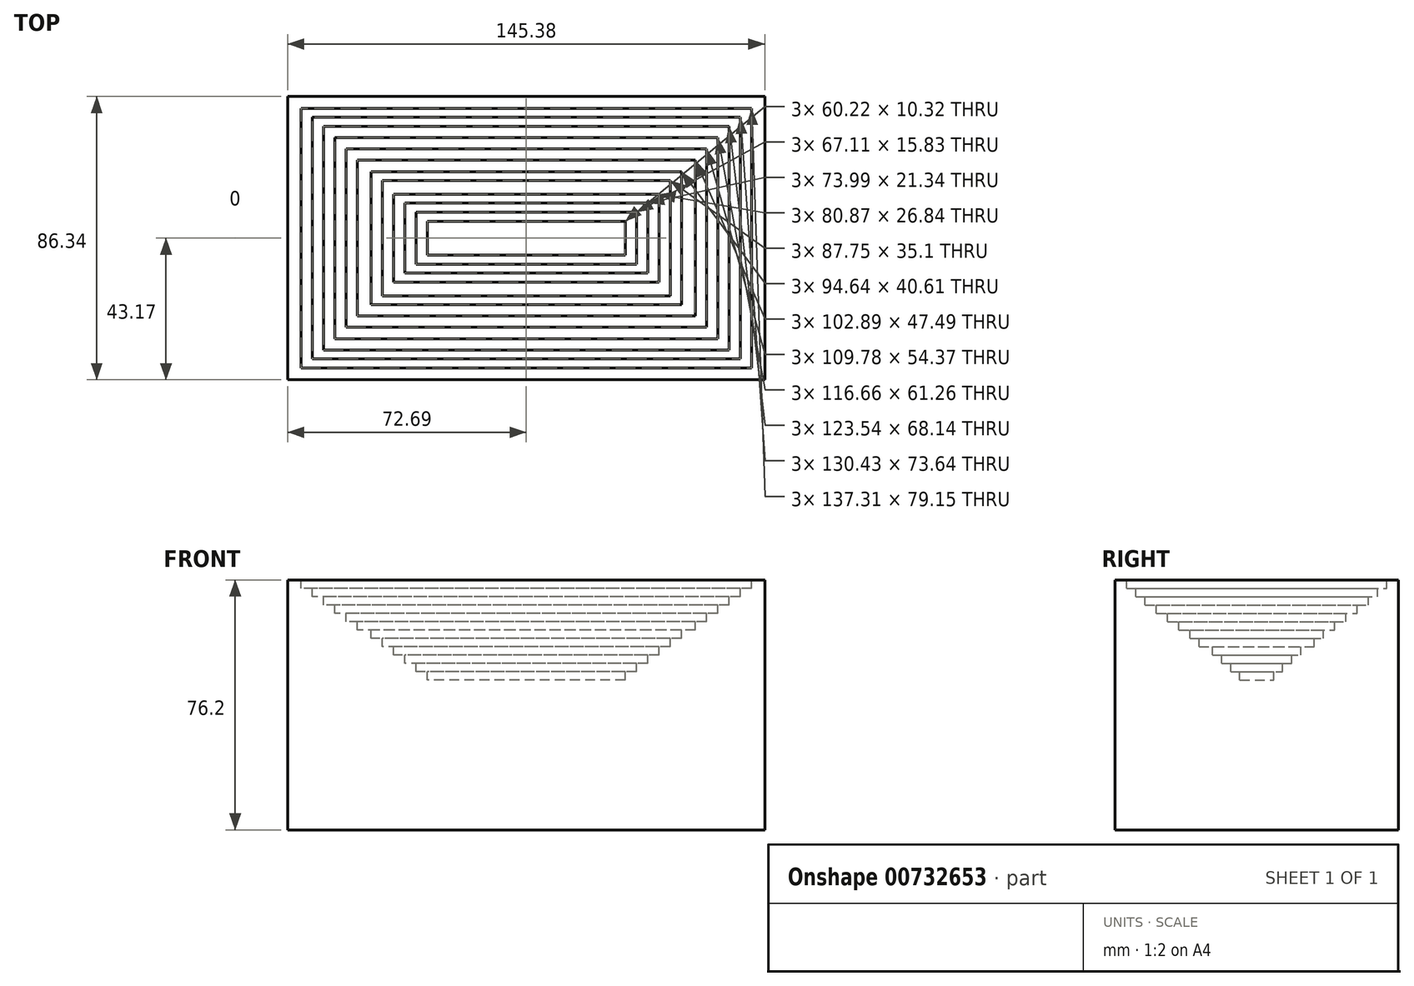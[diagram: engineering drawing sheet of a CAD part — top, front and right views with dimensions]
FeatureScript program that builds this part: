
annotation { "Feature Type Name" : "Feature", "Feature Type Description" : "" }
export const myFeature = defineFeature(function(context is Context, id is Id, definition is map)
    precondition{}
    {
        {
            var Q0;
            Q0=qCreatedBy(makeId("Top.planeOp"),FACE);
            var sketch = newSketch(context, id + "F0", { "sketchPlane" : qUnion([Q0])});
            skLineSegment(sketch, "E0.bottom", {"start": v(72.7, -43.17) * mm, "end": v(-72.7, -43.17) * mm});
            skLineSegment(sketch, "E0.top", {"start": v(72.7, 43.17) * mm, "end": v(-72.7, 43.17) * mm});
            skLineSegment(sketch, "E0.left", {"start": v(72.7, -43.17) * mm, "end": v(72.7, 43.17) * mm});
            skLineSegment(sketch, "E0.right", {"start": v(-72.7, -43.17) * mm, "end": v(-72.7, 43.17) * mm});
            skPoint(sketch, "E0.middle", {"position": v(0, 0) * mm});
            skSolve(sketch);
        }
        {
            var Q0;
            Q0=makeQuery(id+"F0.imprint","IMPRINT",FACE,{"disambiguationData":[TD([[makeQuery(id+"F0.imprint","IMPRINT",EDGE,{"derivedFrom":sQuery(id+"F0.wireOp",EDGE,"E0.bottom")}),-1.0]])]});
            extrude(context, id + "F1", {"entities" : qUnion([Q0]), "depth" : 76.2 * mm, "offsetDistance" : 25.4 * mm});
        }
        {
            var Q0;
            Q0=makeQuery(id+"F1.opExtrude","CAP_FACE",FACE,{"disambiguationData":[OSD([sQuery(id+"F0.wireOp",EDGE,"E0.bottom"),sQuery(id+"F0.wireOp",EDGE,"E0.top"),sQuery(id+"F0.wireOp",EDGE,"E0.left"),sQuery(id+"F0.wireOp",EDGE,"E0.right")])],"isStart":false});
            var sketch = newSketch(context, id + "F2", { "sketchPlane" : qUnion([Q0])});
            skLineSegment(sketch, "E1.bottom", {"start": v(68.65, -39.57) * mm, "end": v(-68.65, -39.57) * mm});
            skLineSegment(sketch, "E1.top", {"start": v(68.65, 39.57) * mm, "end": v(-68.65, 39.57) * mm});
            skLineSegment(sketch, "E1.left", {"start": v(68.65, -39.57) * mm, "end": v(68.65, 39.57) * mm});
            skLineSegment(sketch, "E1.right", {"start": v(-68.65, -39.57) * mm, "end": v(-68.65, 39.57) * mm});
            skPoint(sketch, "E1.middle", {"position": v(0, 0) * mm});
            skSolve(sketch);
        }
        {
            var Q0;
            Q0=makeQuery(id+"F2.imprint","IMPRINT",FACE,{"disambiguationData":[TD([[makeQuery(id+"F2.imprint","IMPRINT",EDGE,{"derivedFrom":sQuery(id+"F2.wireOp",EDGE,"E1.bottom")}),-1.0]])]});
            extrude(context, id + "F3", {"entities" : qUnion([Q0]), "operationType" : NewBodyOperationType.REMOVE, "oppositeDirection" : true, "depth" : 2.54 * mm, "offsetDistance" : 25.4 * mm});
        }
        {
            var Q0;
            Q0=makeQuery(id+"F3.boolean.opBoolean","COPY",FACE,{"derivedFrom":makeQuery(id+"F3.opExtrude","CAP_FACE",FACE,{"disambiguationData":[OSD([sQuery(id+"F2.wireOp",EDGE,"E1.bottom"),sQuery(id+"F2.wireOp",EDGE,"E1.top"),sQuery(id+"F2.wireOp",EDGE,"E1.left"),sQuery(id+"F2.wireOp",EDGE,"E1.right")])],"isStart":false})});
            var sketch = newSketch(context, id + "F4", { "sketchPlane" : qUnion([Q0])});
            skLineSegment(sketch, "E2.bottom", {"start": v(65.21, -36.82) * mm, "end": v(-65.21, -36.82) * mm});
            skLineSegment(sketch, "E2.top", {"start": v(65.21, 36.82) * mm, "end": v(-65.21, 36.82) * mm});
            skLineSegment(sketch, "E2.left", {"start": v(65.21, -36.82) * mm, "end": v(65.21, 36.82) * mm});
            skLineSegment(sketch, "E2.right", {"start": v(-65.21, -36.82) * mm, "end": v(-65.21, 36.82) * mm});
            skPoint(sketch, "E2.middle", {"position": v(0, 0) * mm});
            skSolve(sketch);
        }
        {
            var Q0;
            Q0=makeQuery(id+"F4.imprint","IMPRINT",FACE,{"disambiguationData":[TD([[makeQuery(id+"F4.imprint","IMPRINT",EDGE,{"derivedFrom":sQuery(id+"F4.wireOp",EDGE,"E2.bottom")}),-1.0]])]});
            extrude(context, id + "F5", {"entities" : qUnion([Q0]), "operationType" : NewBodyOperationType.REMOVE, "oppositeDirection" : true, "depth" : 2.54 * mm, "offsetDistance" : 25.4 * mm});
        }
        {
            var Q0;
            Q0=makeQuery(id+"F5.boolean.opBoolean","COPY",FACE,{"derivedFrom":makeQuery(id+"F5.opExtrude","CAP_FACE",FACE,{"disambiguationData":[OSD([sQuery(id+"F4.wireOp",EDGE,"E2.bottom"),sQuery(id+"F4.wireOp",EDGE,"E2.top"),sQuery(id+"F4.wireOp",EDGE,"E2.left"),sQuery(id+"F4.wireOp",EDGE,"E2.right")])],"isStart":false})});
            var sketch = newSketch(context, id + "F6", { "sketchPlane" : qUnion([Q0])});
            skLineSegment(sketch, "E3.bottom", {"start": v(61.77, -34.07) * mm, "end": v(-61.77, -34.07) * mm});
            skLineSegment(sketch, "E3.top", {"start": v(61.77, 34.07) * mm, "end": v(-61.77, 34.07) * mm});
            skLineSegment(sketch, "E3.left", {"start": v(61.77, -34.07) * mm, "end": v(61.77, 34.07) * mm});
            skLineSegment(sketch, "E3.right", {"start": v(-61.77, -34.07) * mm, "end": v(-61.77, 34.07) * mm});
            skPoint(sketch, "E3.middle", {"position": v(0, 0) * mm});
            skSolve(sketch);
        }
        {
            var Q0;
            Q0=makeQuery(id+"F6.imprint","IMPRINT",FACE,{"disambiguationData":[TD([[makeQuery(id+"F6.imprint","IMPRINT",EDGE,{"derivedFrom":sQuery(id+"F6.wireOp",EDGE,"E3.bottom")}),-1.0]])]});
            extrude(context, id + "F7", {"entities" : qUnion([Q0]), "operationType" : NewBodyOperationType.REMOVE, "oppositeDirection" : true, "depth" : 2.54 * mm, "offsetDistance" : 25.4 * mm});
        }
        {
            var Q0;
            Q0=makeQuery(id+"F7.boolean.opBoolean","COPY",FACE,{"derivedFrom":makeQuery(id+"F7.opExtrude","CAP_FACE",FACE,{"disambiguationData":[OSD([sQuery(id+"F6.wireOp",EDGE,"E3.bottom"),sQuery(id+"F6.wireOp",EDGE,"E3.top"),sQuery(id+"F6.wireOp",EDGE,"E3.left"),sQuery(id+"F6.wireOp",EDGE,"E3.right")])],"isStart":false})});
            var sketch = newSketch(context, id + "F8", { "sketchPlane" : qUnion([Q0])});
            skLineSegment(sketch, "E4.bottom", {"start": v(58.33, -30.63) * mm, "end": v(-58.33, -30.63) * mm});
            skLineSegment(sketch, "E4.top", {"start": v(58.33, 30.63) * mm, "end": v(-58.33, 30.63) * mm});
            skLineSegment(sketch, "E4.left", {"start": v(58.33, -30.63) * mm, "end": v(58.33, 30.63) * mm});
            skLineSegment(sketch, "E4.right", {"start": v(-58.33, -30.63) * mm, "end": v(-58.33, 30.63) * mm});
            skPoint(sketch, "E4.middle", {"position": v(0, 0) * mm});
            skSolve(sketch);
        }
        {
            var Q0;
            Q0=makeQuery(id+"F8.imprint","IMPRINT",FACE,{"disambiguationData":[TD([[makeQuery(id+"F8.imprint","IMPRINT",EDGE,{"derivedFrom":sQuery(id+"F8.wireOp",EDGE,"E4.bottom")}),-1.0]])]});
            extrude(context, id + "F9", {"entities" : qUnion([Q0]), "operationType" : NewBodyOperationType.REMOVE, "oppositeDirection" : true, "depth" : 2.54 * mm, "offsetDistance" : 25.4 * mm});
        }
        {
            var Q0;
            Q0=makeQuery(id+"F9.boolean.opBoolean","COPY",FACE,{"derivedFrom":makeQuery(id+"F9.opExtrude","CAP_FACE",FACE,{"disambiguationData":[OSD([sQuery(id+"F8.wireOp",EDGE,"E4.bottom"),sQuery(id+"F8.wireOp",EDGE,"E4.top"),sQuery(id+"F8.wireOp",EDGE,"E4.left"),sQuery(id+"F8.wireOp",EDGE,"E4.right")])],"isStart":false})});
            var sketch = newSketch(context, id + "F10", { "sketchPlane" : qUnion([Q0])});
            skLineSegment(sketch, "E5.bottom", {"start": v(54.89, -27.19) * mm, "end": v(-54.89, -27.19) * mm});
            skLineSegment(sketch, "E5.top", {"start": v(54.89, 27.19) * mm, "end": v(-54.89, 27.19) * mm});
            skLineSegment(sketch, "E5.left", {"start": v(54.89, -27.19) * mm, "end": v(54.89, 27.19) * mm});
            skLineSegment(sketch, "E5.right", {"start": v(-54.89, -27.19) * mm, "end": v(-54.89, 27.19) * mm});
            skPoint(sketch, "E5.middle", {"position": v(0, 0) * mm});
            skSolve(sketch);
        }
        {
            var Q0;
            Q0=makeQuery(id+"F10.imprint","IMPRINT",FACE,{"disambiguationData":[TD([[makeQuery(id+"F10.imprint","IMPRINT",EDGE,{"derivedFrom":sQuery(id+"F10.wireOp",EDGE,"E5.bottom")}),-1.0]])]});
            extrude(context, id + "F11", {"entities" : qUnion([Q0]), "operationType" : NewBodyOperationType.REMOVE, "oppositeDirection" : true, "depth" : 2.54 * mm, "offsetDistance" : 25.4 * mm});
        }
        {
            var Q0;
            Q0=makeQuery(id+"F11.boolean.opBoolean","COPY",FACE,{"derivedFrom":makeQuery(id+"F11.opExtrude","CAP_FACE",FACE,{"disambiguationData":[OSD([sQuery(id+"F10.wireOp",EDGE,"E5.bottom"),sQuery(id+"F10.wireOp",EDGE,"E5.top"),sQuery(id+"F10.wireOp",EDGE,"E5.left"),sQuery(id+"F10.wireOp",EDGE,"E5.right")])],"isStart":false})});
            var sketch = newSketch(context, id + "F12", { "sketchPlane" : qUnion([Q0])});
            skLineSegment(sketch, "E6.bottom", {"start": v(51.45, -23.74) * mm, "end": v(-51.45, -23.74) * mm});
            skLineSegment(sketch, "E6.top", {"start": v(51.45, 23.74) * mm, "end": v(-51.45, 23.74) * mm});
            skLineSegment(sketch, "E6.left", {"start": v(51.45, -23.74) * mm, "end": v(51.45, 23.74) * mm});
            skLineSegment(sketch, "E6.right", {"start": v(-51.45, -23.74) * mm, "end": v(-51.45, 23.74) * mm});
            skPoint(sketch, "E6.middle", {"position": v(0, 0) * mm});
            skSolve(sketch);
        }
        {
            var Q0;
            Q0=makeQuery(id+"F12.imprint","IMPRINT",FACE,{"disambiguationData":[TD([[makeQuery(id+"F12.imprint","IMPRINT",EDGE,{"derivedFrom":sQuery(id+"F12.wireOp",EDGE,"E6.bottom")}),-1.0]])]});
            extrude(context, id + "F13", {"entities" : qUnion([Q0]), "operationType" : NewBodyOperationType.REMOVE, "oppositeDirection" : true, "depth" : 2.54 * mm, "offsetDistance" : 25.4 * mm});
        }
        {
            var Q0;
            Q0=makeQuery(id+"F13.boolean.opBoolean","COPY",FACE,{"derivedFrom":makeQuery(id+"F13.opExtrude","CAP_FACE",FACE,{"disambiguationData":[OSD([sQuery(id+"F12.wireOp",EDGE,"E6.bottom"),sQuery(id+"F12.wireOp",EDGE,"E6.top"),sQuery(id+"F12.wireOp",EDGE,"E6.left"),sQuery(id+"F12.wireOp",EDGE,"E6.right")])],"isStart":false})});
            var sketch = newSketch(context, id + "F14", { "sketchPlane" : qUnion([Q0])});
            skLineSegment(sketch, "E7.bottom", {"start": v(47.32, -20.3) * mm, "end": v(-47.32, -20.3) * mm});
            skLineSegment(sketch, "E7.top", {"start": v(47.32, 20.3) * mm, "end": v(-47.32, 20.3) * mm});
            skLineSegment(sketch, "E7.left", {"start": v(47.32, -20.3) * mm, "end": v(47.32, 20.3) * mm});
            skLineSegment(sketch, "E7.right", {"start": v(-47.32, -20.3) * mm, "end": v(-47.32, 20.3) * mm});
            skPoint(sketch, "E7.middle", {"position": v(0, 0) * mm});
            skSolve(sketch);
        }
        {
            var Q0;
            Q0=makeQuery(id+"F14.imprint","IMPRINT",FACE,{"disambiguationData":[TD([[makeQuery(id+"F14.imprint","IMPRINT",EDGE,{"derivedFrom":sQuery(id+"F14.wireOp",EDGE,"E7.bottom")}),-1.0]])]});
            extrude(context, id + "F15", {"entities" : qUnion([Q0]), "operationType" : NewBodyOperationType.REMOVE, "oppositeDirection" : true, "depth" : 2.54 * mm, "offsetDistance" : 25.4 * mm});
        }
        {
            var Q0;
            Q0=makeQuery(id+"F15.boolean.opBoolean","COPY",FACE,{"derivedFrom":makeQuery(id+"F15.opExtrude","CAP_FACE",FACE,{"disambiguationData":[OSD([sQuery(id+"F14.wireOp",EDGE,"E7.bottom"),sQuery(id+"F14.wireOp",EDGE,"E7.top"),sQuery(id+"F14.wireOp",EDGE,"E7.left"),sQuery(id+"F14.wireOp",EDGE,"E7.right")])],"isStart":false})});
            var sketch = newSketch(context, id + "F16", { "sketchPlane" : qUnion([Q0])});
            skLineSegment(sketch, "E8.bottom", {"start": v(43.88, -17.55) * mm, "end": v(-43.88, -17.55) * mm});
            skLineSegment(sketch, "E8.top", {"start": v(43.88, 17.55) * mm, "end": v(-43.88, 17.55) * mm});
            skLineSegment(sketch, "E8.left", {"start": v(43.88, -17.55) * mm, "end": v(43.88, 17.55) * mm});
            skLineSegment(sketch, "E8.right", {"start": v(-43.88, -17.55) * mm, "end": v(-43.88, 17.55) * mm});
            skPoint(sketch, "E8.middle", {"position": v(0, 0) * mm});
            skSolve(sketch);
        }
        {
            var Q0;
            Q0=makeQuery(id+"F16.imprint","IMPRINT",FACE,{"disambiguationData":[TD([[makeQuery(id+"F16.imprint","IMPRINT",EDGE,{"derivedFrom":sQuery(id+"F16.wireOp",EDGE,"E8.bottom")}),-1.0]])]});
            extrude(context, id + "F17", {"entities" : qUnion([Q0]), "operationType" : NewBodyOperationType.REMOVE, "oppositeDirection" : true, "depth" : 2.54 * mm, "offsetDistance" : 25.4 * mm});
        }
        {
            var Q0;
            Q0=makeQuery(id+"F17.boolean.opBoolean","COPY",FACE,{"derivedFrom":makeQuery(id+"F17.opExtrude","CAP_FACE",FACE,{"disambiguationData":[OSD([sQuery(id+"F16.wireOp",EDGE,"E8.bottom"),sQuery(id+"F16.wireOp",EDGE,"E8.top"),sQuery(id+"F16.wireOp",EDGE,"E8.left"),sQuery(id+"F16.wireOp",EDGE,"E8.right")])],"isStart":false})});
            var sketch = newSketch(context, id + "F18", { "sketchPlane" : qUnion([Q0])});
            skLineSegment(sketch, "E9.bottom", {"start": v(40.44, -13.42) * mm, "end": v(-40.44, -13.42) * mm});
            skLineSegment(sketch, "E9.top", {"start": v(40.44, 13.42) * mm, "end": v(-40.44, 13.42) * mm});
            skLineSegment(sketch, "E9.left", {"start": v(40.44, -13.42) * mm, "end": v(40.44, 13.42) * mm});
            skLineSegment(sketch, "E9.right", {"start": v(-40.44, -13.42) * mm, "end": v(-40.44, 13.42) * mm});
            skPoint(sketch, "E9.middle", {"position": v(0, 0) * mm});
            skSolve(sketch);
        }
        {
            var Q0;
            Q0=makeQuery(id+"F18.imprint","IMPRINT",FACE,{"disambiguationData":[TD([[makeQuery(id+"F18.imprint","IMPRINT",EDGE,{"derivedFrom":sQuery(id+"F18.wireOp",EDGE,"E9.bottom")}),-1.0]])]});
            extrude(context, id + "F19", {"entities" : qUnion([Q0]), "operationType" : NewBodyOperationType.REMOVE, "oppositeDirection" : true, "depth" : 2.54 * mm, "offsetDistance" : 25.4 * mm});
        }
        {
            var Q0;
            Q0=makeQuery(id+"F19.boolean.opBoolean","COPY",FACE,{"derivedFrom":makeQuery(id+"F19.opExtrude","CAP_FACE",FACE,{"disambiguationData":[OSD([sQuery(id+"F18.wireOp",EDGE,"E9.bottom"),sQuery(id+"F18.wireOp",EDGE,"E9.top"),sQuery(id+"F18.wireOp",EDGE,"E9.left"),sQuery(id+"F18.wireOp",EDGE,"E9.right")])],"isStart":false})});
            var sketch = newSketch(context, id + "F20", { "sketchPlane" : qUnion([Q0])});
            skLineSegment(sketch, "E10.bottom", {"start": v(37, -10.67) * mm, "end": v(-37, -10.67) * mm});
            skLineSegment(sketch, "E10.top", {"start": v(37, 10.67) * mm, "end": v(-37, 10.67) * mm});
            skLineSegment(sketch, "E10.left", {"start": v(37, -10.67) * mm, "end": v(37, 10.67) * mm});
            skLineSegment(sketch, "E10.right", {"start": v(-37, -10.67) * mm, "end": v(-37, 10.67) * mm});
            skPoint(sketch, "E10.middle", {"position": v(0, 0) * mm});
            skSolve(sketch);
        }
        {
            var Q0;
            Q0=makeQuery(id+"F20.imprint","IMPRINT",FACE,{"disambiguationData":[TD([[makeQuery(id+"F20.imprint","IMPRINT",EDGE,{"derivedFrom":sQuery(id+"F20.wireOp",EDGE,"E10.bottom")}),-1.0]])]});
            extrude(context, id + "F21", {"entities" : qUnion([Q0]), "operationType" : NewBodyOperationType.REMOVE, "oppositeDirection" : true, "depth" : 2.54 * mm, "offsetDistance" : 25.4 * mm});
        }
        {
            var Q0;
            Q0=makeQuery(id+"F21.boolean.opBoolean","COPY",FACE,{"derivedFrom":makeQuery(id+"F21.opExtrude","CAP_FACE",FACE,{"disambiguationData":[OSD([sQuery(id+"F20.wireOp",EDGE,"E10.bottom"),sQuery(id+"F20.wireOp",EDGE,"E10.top"),sQuery(id+"F20.wireOp",EDGE,"E10.left"),sQuery(id+"F20.wireOp",EDGE,"E10.right")])],"isStart":false})});
            var sketch = newSketch(context, id + "F22", { "sketchPlane" : qUnion([Q0])});
            skLineSegment(sketch, "E11.bottom", {"start": v(33.55, -7.91) * mm, "end": v(-33.55, -7.91) * mm});
            skLineSegment(sketch, "E11.top", {"start": v(33.55, 7.91) * mm, "end": v(-33.55, 7.91) * mm});
            skLineSegment(sketch, "E11.left", {"start": v(33.55, -7.91) * mm, "end": v(33.55, 7.91) * mm});
            skLineSegment(sketch, "E11.right", {"start": v(-33.55, -7.91) * mm, "end": v(-33.55, 7.91) * mm});
            skPoint(sketch, "E11.middle", {"position": v(0, 0) * mm});
            skSolve(sketch);
        }
        {
            var Q0;
            Q0=makeQuery(id+"F22.imprint","IMPRINT",FACE,{"disambiguationData":[TD([[makeQuery(id+"F22.imprint","IMPRINT",EDGE,{"derivedFrom":sQuery(id+"F22.wireOp",EDGE,"E11.bottom")}),-1.0]])]});
            extrude(context, id + "F23", {"entities" : qUnion([Q0]), "operationType" : NewBodyOperationType.REMOVE, "oppositeDirection" : true, "depth" : 2.54 * mm, "offsetDistance" : 25.4 * mm});
        }
        {
            var Q0;
            Q0=makeQuery(id+"F23.boolean.opBoolean","COPY",FACE,{"derivedFrom":makeQuery(id+"F23.opExtrude","CAP_FACE",FACE,{"disambiguationData":[OSD([sQuery(id+"F22.wireOp",EDGE,"E11.bottom"),sQuery(id+"F22.wireOp",EDGE,"E11.top"),sQuery(id+"F22.wireOp",EDGE,"E11.left"),sQuery(id+"F22.wireOp",EDGE,"E11.right")])],"isStart":false})});
            var sketch = newSketch(context, id + "F24", { "sketchPlane" : qUnion([Q0])});
            skLineSegment(sketch, "E12.bottom", {"start": v(30.11, -5.16) * mm, "end": v(-30.11, -5.16) * mm});
            skLineSegment(sketch, "E12.top", {"start": v(30.11, 5.16) * mm, "end": v(-30.11, 5.16) * mm});
            skLineSegment(sketch, "E12.left", {"start": v(30.11, -5.16) * mm, "end": v(30.11, 5.16) * mm});
            skLineSegment(sketch, "E12.right", {"start": v(-30.11, -5.16) * mm, "end": v(-30.11, 5.16) * mm});
            skPoint(sketch, "E12.middle", {"position": v(0, 0) * mm});
            skSolve(sketch);
        }
        {
            var Q0;
            Q0=makeQuery(id+"F24.imprint","IMPRINT",FACE,{"disambiguationData":[TD([[makeQuery(id+"F24.imprint","IMPRINT",EDGE,{"derivedFrom":sQuery(id+"F24.wireOp",EDGE,"E12.bottom")}),-1.0]])]});
            extrude(context, id + "F25", {"entities" : qUnion([Q0]), "operationType" : NewBodyOperationType.REMOVE, "oppositeDirection" : true, "depth" : 2.54 * mm, "offsetDistance" : 25.4 * mm});
        }
    });
